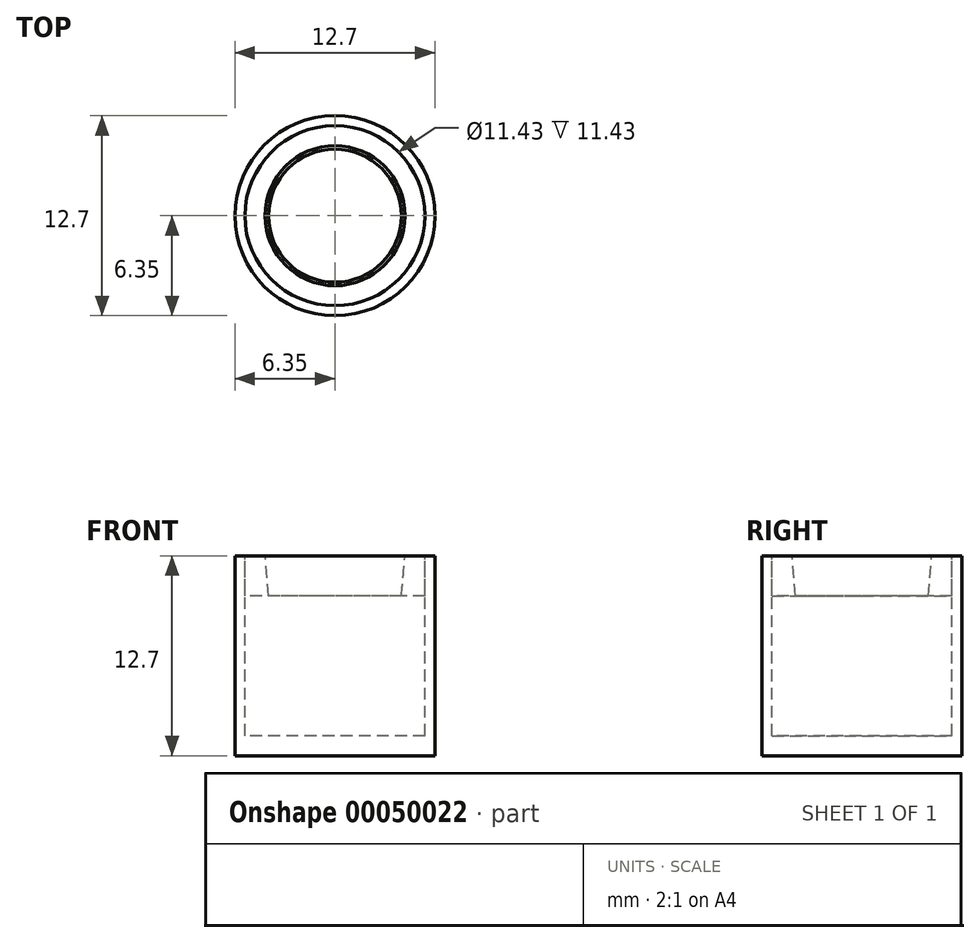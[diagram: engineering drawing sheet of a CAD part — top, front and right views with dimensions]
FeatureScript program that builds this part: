
annotation { "Feature Type Name" : "Feature", "Feature Type Description" : "" }
export const myFeature = defineFeature(function(context is Context, id is Id, definition is map)
    precondition{}
    {
        {
            var Q0;
            Q0=qCreatedBy(makeId("Top.planeOp"),FACE);
            var sketch = newSketch(context, id + "F0", { "sketchPlane" : qUnion([Q0])});
            skCircle(sketch, "E0", {"center": v(0, 0) * mm, "radius": 6.35 * mm});
            skSolve(sketch);
        }
        {
            var Q0;
            Q0=makeQuery(id+"F0.imprint","IMPRINT",FACE,{"disambiguationData":[TD([[makeQuery(id+"F0.imprint","IMPRINT",EDGE,{"derivedFrom":sQuery(id+"F0.wireOp",EDGE,"E0")}),1.0]])]});
            extrude(context, id + "F1", {"entities" : qUnion([Q0]), "depth" : 12.7 * mm});
        }
        {
            var Q0;
            Q0=makeQuery(id+"F1.opExtrude","CAP_FACE",FACE,{"disambiguationData":[OSD([sQuery(id+"F0.wireOp",EDGE,"E0")])],"isStart":false});
            var sketch = newSketch(context, id + "F2", { "sketchPlane" : qUnion([Q0])});
            skCircle(sketch, "E1", {"center": v(0, 0) * mm, "radius": 5.72 * mm});
            skCircle(sketch, "E2", {"center": v(0, 0) * mm, "radius": 4.45 * mm});
            skSolve(sketch);
        }
        {
            var Q0;
            Q0=makeQuery(id+"F2.imprint","IMPRINT",FACE,{"disambiguationData":[TD([[makeQuery(id+"F2.imprint","IMPRINT",EDGE,{"derivedFrom":sQuery(id+"F2.wireOp",EDGE,"E1")}),1.0]])]});
            extrude(context, id + "F3", {"entities" : qUnion([Q0]), "operationType" : NewBodyOperationType.REMOVE, "oppositeDirection" : true, "depth" : 11.43 * mm});
        }
        {
            var Q0;
            Q0=makeQuery(id+"F2.imprint","IMPRINT",FACE,{"disambiguationData":[TD([[makeQuery(id+"F2.imprint","IMPRINT",EDGE,{"derivedFrom":sQuery(id+"F2.wireOp",EDGE,"E1")}),1.0]])]});
            extrude(context, id + "F4", {"entities" : qUnion([Q0]), "oppositeDirection" : true, "depth" : 2.54 * mm});
        }
        {
            var Q0;
            Q0=makeQuery(id+"F2.imprint","IMPRINT",FACE,{"disambiguationData":[TD([[makeQuery(id+"F2.imprint","IMPRINT",EDGE,{"derivedFrom":sQuery(id+"F2.wireOp",EDGE,"E2")}),1.0]])]});
            extrude(context, id + "F5", {"entities" : qUnion([Q0]), "operationType" : NewBodyOperationType.REMOVE, "oppositeDirection" : true, "depth" : 11.43 * mm});
        }
        {
            var Q0;
            Q0=makeQuery(id+"F2.imprint","IMPRINT",FACE,{"disambiguationData":[TD([[makeQuery(id+"F2.imprint","IMPRINT",EDGE,{"derivedFrom":sQuery(id+"F2.wireOp",EDGE,"E2")}),1.0]])]});
            extrude(context, id + "F6", {"entities" : qUnion([Q0]), "operationType" : NewBodyOperationType.ADD, "oppositeDirection" : true, "depth" : 2.54 * mm});
        }
        {
            var Q0;
            Q0=makeQuery(id+"F2.imprint","IMPRINT",FACE,{"disambiguationData":[TD([[makeQuery(id+"F2.imprint","IMPRINT",EDGE,{"derivedFrom":sQuery(id+"F2.wireOp",EDGE,"E2")}),1.0]])]});
            extrude(context, id + "F7", {"entities" : qUnion([Q0]), "operationType" : NewBodyOperationType.REMOVE, "oppositeDirection" : true, "depth" : 2.54 * mm, "hasDraft" : true, "draftAngle" : 5 * degree, "draftPullDirection" : true});
        }
    });
